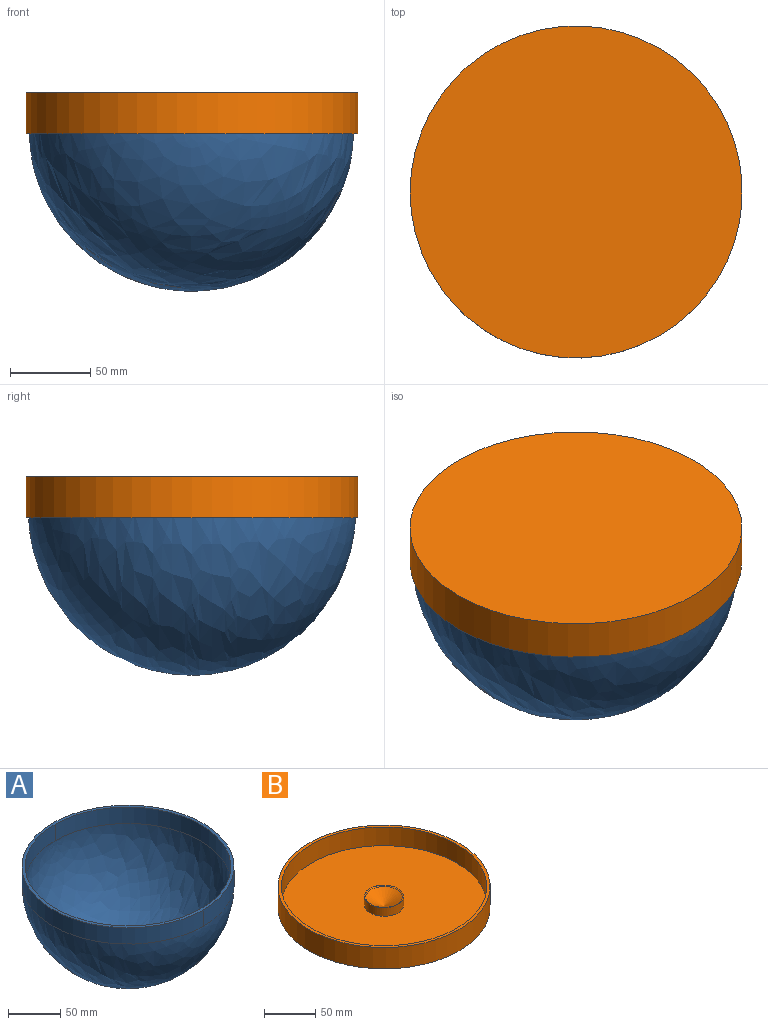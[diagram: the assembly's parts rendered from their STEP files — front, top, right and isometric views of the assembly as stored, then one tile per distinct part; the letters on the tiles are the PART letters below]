
ASSEMBLY  parts=2 mates=1
PART A: 7 faces, bbox 202.3x203.2x120.2 mm
  f0: revolved ~203.2x202.27mm, area 64393.7mm2, adj f2,f3
  f1: cylinder r=98.42mm len=196.85mm, axis (0,0,-1), area 5872.8mm2, adj f4,f5,f6
  f2: cylinder r=101.6mm len=203.2mm, axis (0,0,-1), area 6062.8mm2, adj f0,f3,f5
  f3: cylinder r=101.6mm len=203.2mm, axis (0,0,-1), area 6062.8mm2, adj f0,f2,f5
  f4: cylinder r=98.42mm len=196.85mm, axis (0,0,-1), area 5872.8mm2, adj f1,f5,f6
  f5: plane 203.2x202.27mm, normal (0,0,1), area 1989.3mm2, adj f1,f2,f3,f4
  f6: revolved ~196.85x195.92mm, area 60417.9mm2, adj f1,f4
PART B: 9 faces, bbox 206.4x206.4x25.4 mm
  f0: cylinder r=103.19mm len=206.38mm, axis (0,0,-1), area 16468mm2, adj f1,f2
  f1: plane 206.38x206.38mm, normal (0,0,1), area 2026.8mm2, adj f0,f3
  f2: plane 206.38x206.38mm, normal (0,0,-1), area 33450.6mm2, adj f0
  f3: cylinder r=100.01mm len=200.03mm, axis (0,0,-1), area 13966.1mm2, adj f1,f4
  f4: plane 200.03x200.03mm, normal (0,0,1), area 30283.7mm2, adj f3,f5
  f5: cylinder r=19.05mm len=38.1mm, axis (0,0,-1), area 1216.1mm2, adj f4,f6
  f6: plane 38.1x38.1mm, normal (0,0,1), area 12.7mm2, adj f5,f8
  f7: cone r=0mm half-angle=59deg, axis (0,0,1), area 1158.6mm2, adj f8
  f8: torus R=18.94mm, axis (0,0,1), area 169.2mm2, adj f6,f7
PLACE A at identity
PLACE B rot(axis=(0,-1,0),180deg) t=(0.46,0,22.22)mm
MATE fastened B.f0 <-> A.f1  axis (0,0,-1) through (0.46,0,19.05)mm
